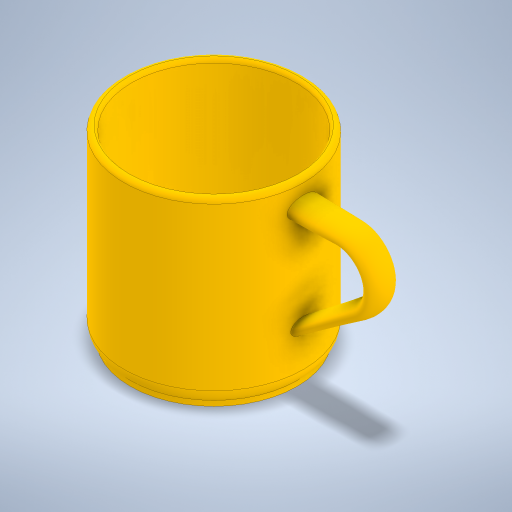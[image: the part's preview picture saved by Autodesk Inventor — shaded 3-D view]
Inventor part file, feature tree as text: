
AUTODESK INVENTOR PART (.ipt)
format: ipt  version: 2024 (Build 280153000, 153)  size: 398,848 bytes
history: native  units: mm
features: other x5, sketch x5, plane x3, revolve x1, shell x1, loft x1, fillet x1, extrude x1
ambient origin geometry x8: Origin, YZ Plane, XZ Plane, XY Plane, X Axis, Y Axis, Z Axis, Center Point
bodies: Body1 (feature_tree)
feature tree (18):
  other  "Sección transversal1"
  other  "Sección transversal2"
  other  "Sección transversal3"
  revolve  "Revolución2"  [1 undecoded]
  shell  "Vaciado1"  Thickness=65.0mm
  sketch  "Boceto3"  dims[d8=32.5mm d9=90.0deg d10=3.0mm]
  plane  "Plano de trabajo4"
  sketch  "Boceto10"  dims[d11=0.5mm d12=2.0mm d13=0.0mm d14=20.0mm]
  plane  "Plano de trabajo5"
  other  "Punto de trabajo6"
  plane  "Plano de trabajo8"
  loft  "Solevación1"
  fillet  "Empalme1"  Radius=3.0mm
  extrude  "Extrusión1"  Depth=2.0mm
  sketch  "Boceto2"  dims[d5=70.0mm d6=35.0mm d7=65.0mm]
  other  "Punto de trabajo5"
  sketch  "Boceto12"  dims[d31=0.5mm d32=2.0mm d33=0.0mm d34=20.0mm d35=0.5mm d36=2.0mm d37=0.0mm d38=20.0mm d39=4.0mm]
  sketch  "Boceto13"  dims[d40=6.0mm d45=25.0mm d46=12.0mm d47=15.0mm d50=3.0mm d51=5.0mm d52=0.0mm d53=90.0deg d54=0.0mm d55=90.0deg d56=0.0mm d57=90.0deg d58=2.0mm d59=65.0mm d60=62.0mm d61=2.0mm d62=0.0mm d4=0.872665mm]
note: 1 required parameter value undecoded (feature->parameter linkage not recoverable at this tier; creation-order binding heuristic only, values carry confidence <= 0.55)
